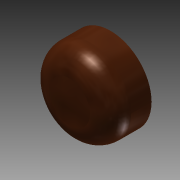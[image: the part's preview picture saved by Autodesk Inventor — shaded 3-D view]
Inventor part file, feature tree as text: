
AUTODESK INVENTOR PART (.ipt)
format: ipt  version: 2015 (Build 190159000, 159)  size: 103,424 bytes
history: native  units: in
note: dims shown in document units (in); Inventor stores cm internally (conversion verified against a paired STEP export)
features: extrude x1, fillet x1, sketch x1
ambient origin geometry x8: Origin, YZ Plane, XZ Plane, XY Plane, X Axis, Y Axis, Z Axis, Center Point
bodies: Solid1 (feature_tree)
feature tree (3):
  extrude  "Extrusion1"  Depth=0.125in TaperAngle=0.0deg
  fillet  "Fillet1"  Radius=0.0625in
  sketch  "Sketch1"  dims[d0=0.25in d1=0.125in d2=0.0in d3=0.0625in]
